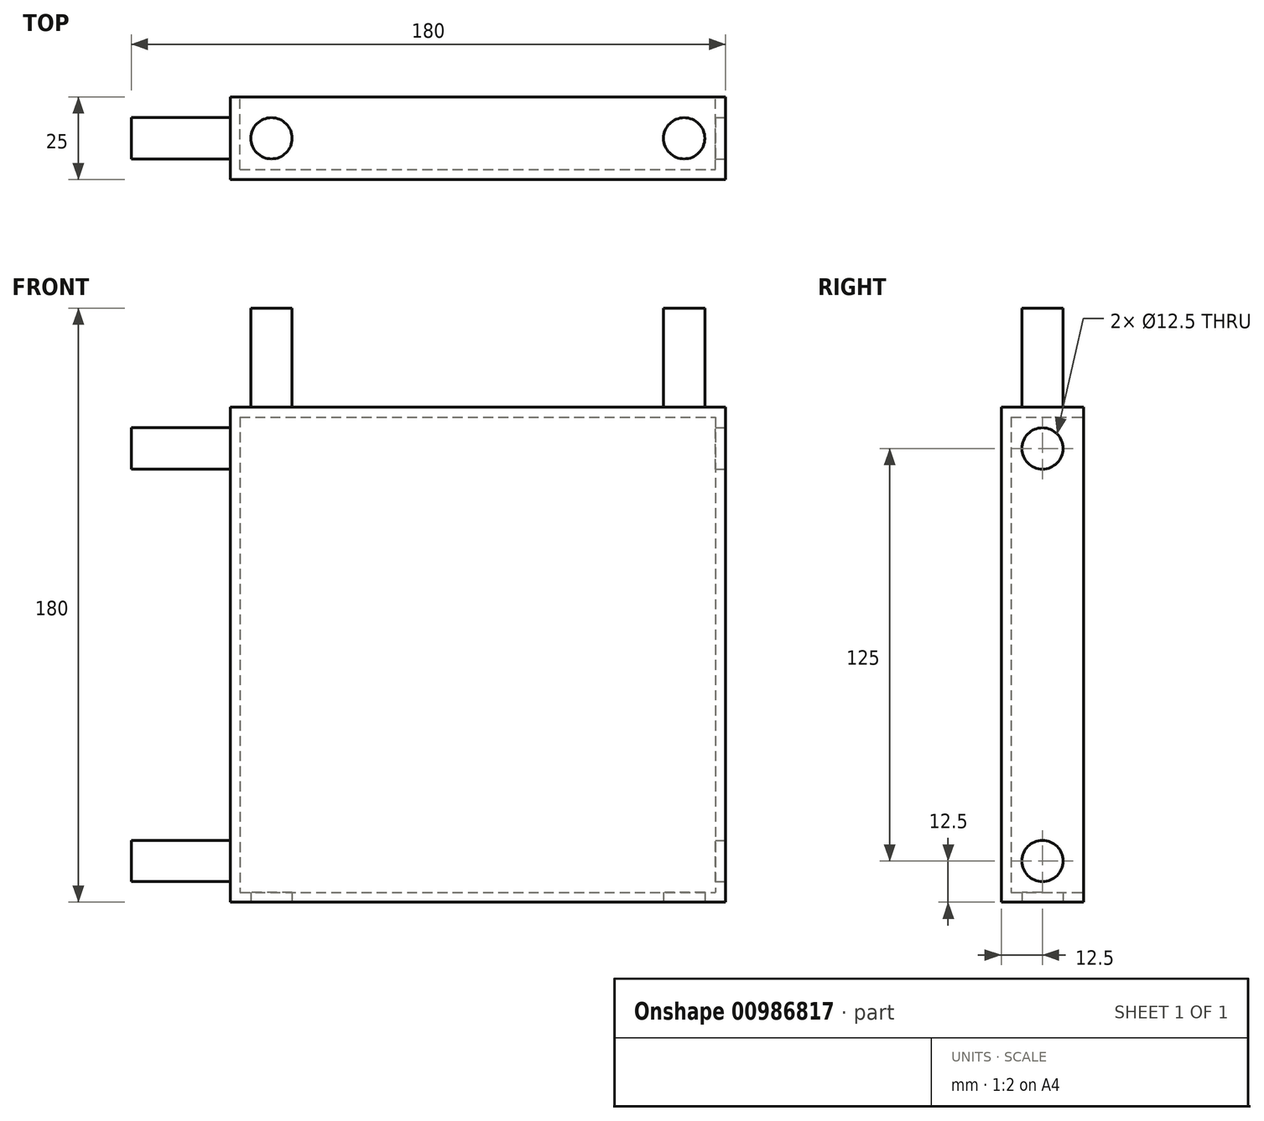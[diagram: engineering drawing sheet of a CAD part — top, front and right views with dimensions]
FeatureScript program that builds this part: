
annotation { "Feature Type Name" : "Feature", "Feature Type Description" : "" }
export const myFeature = defineFeature(function(context is Context, id is Id, definition is map)
    precondition{}
    {
        {
            var Q0;
            Q0=qCreatedBy(makeId("Front.planeOp"),FACE);
            var sketch = newSketch(context, id + "F0", { "sketchPlane" : qUnion([Q0])});
            skLineSegment(sketch, "E0.bottom", {"start": v(-87.46, 78.58) * mm, "end": v(62.54, 78.58) * mm});
            skLineSegment(sketch, "E0.top", {"start": v(-87.46, -71.42) * mm, "end": v(62.54, -71.42) * mm});
            skLineSegment(sketch, "E0.left", {"start": v(-87.46, 78.58) * mm, "end": v(-87.46, -71.42) * mm});
            skLineSegment(sketch, "E0.right", {"start": v(62.54, 78.58) * mm, "end": v(62.54, -71.42) * mm});
            skSolve(sketch);
        }
        {
            var Q0;
            Q0=makeQuery(id+"F0.imprint","IMPRINT",FACE,{"disambiguationData":[TD([[makeQuery(id+"F0.imprint","IMPRINT",EDGE,{"derivedFrom":sQuery(id+"F0.wireOp",EDGE,"E0.bottom")}),-1.0]])]});
            extrude(context, id + "F1", {"entities" : qUnion([Q0]), "depth" : 25 * mm, "offsetDistance" : 25 * mm});
        }
        {
            var Q0;
            Q0=makeQuery(id+"F1.opExtrude","CAP_FACE",FACE,{"disambiguationData":[OSD([sQuery(id+"F0.wireOp",EDGE,"E0.bottom"),sQuery(id+"F0.wireOp",EDGE,"E0.top"),sQuery(id+"F0.wireOp",EDGE,"E0.left"),sQuery(id+"F0.wireOp",EDGE,"E0.right")])],"isStart":true});
            shell(context, id + "F2", {"entities" : qUnion([Q0]), "thickness" : 3 * mm});
        }
        {
            var Q0;
            Q0=makeQuery(id+"F1.opExtrude","SWEPT_FACE",FACE,{"disambiguationData":[OSD([sQuery(id+"F0.wireOp",EDGE,"E0.bottom")])]});
            var sketch = newSketch(context, id + "F3", { "sketchPlane" : qUnion([Q0])});
            skCircle(sketch, "E1", {"center": v(-74.96, -12.5) * mm, "radius": 6.25 * mm});
            skCircle(sketch, "E2", {"center": v(50.04, -12.5) * mm, "radius": 6.25 * mm});
            skSolve(sketch);
        }
        {
            var Q0;
            Q0 = qSketchRegion(id + "F3", true);
            extrude(context, id + "F4", {"entities" : qUnion([Q0]), "operationType" : NewBodyOperationType.ADD, "depth" : 30 * mm, "offsetDistance" : 25 * mm});
        }
        {
            var Q0;
            Q0=makeQuery(id+"F1.opExtrude","SWEPT_FACE",FACE,{"disambiguationData":[OSD([sQuery(id+"F0.wireOp",EDGE,"E0.top")])]});
            var sketch = newSketch(context, id + "F5", { "sketchPlane" : qUnion([Q0])});
            skCircle(sketch, "E3", {"center": v(-74.96, 12.5) * mm, "radius": 6.25 * mm});
            skCircle(sketch, "E4", {"center": v(50.04, 12.5) * mm, "radius": 6.25 * mm});
            skSolve(sketch);
        }
        {
            var Q0;
            Q0 = qSketchRegion(id + "F5", true);
            extrude(context, id + "F6", {"entities" : qUnion([Q0]), "operationType" : NewBodyOperationType.REMOVE, "oppositeDirection" : true, "depth" : 25 * mm, "offsetDistance" : 25 * mm});
        }
        {
            var Q0;
            Q0=makeQuery(id+"F1.opExtrude","SWEPT_FACE",FACE,{"disambiguationData":[OSD([sQuery(id+"F0.wireOp",EDGE,"E0.left")])]});
            var sketch = newSketch(context, id + "F7", { "sketchPlane" : qUnion([Q0])});
            skCircle(sketch, "E5", {"center": v(12.5, 66.08) * mm, "radius": 6.25 * mm});
            skCircle(sketch, "E6", {"center": v(12.5, -58.92) * mm, "radius": 6.25 * mm});
            skSolve(sketch);
        }
        {
            var Q0;
            Q0 = qSketchRegion(id + "F7", true);
            extrude(context, id + "F8", {"entities" : qUnion([Q0]), "operationType" : NewBodyOperationType.ADD, "depth" : 30 * mm, "offsetDistance" : 25 * mm});
        }
        {
            var Q0;
            Q0=makeQuery(id+"F1.opExtrude","SWEPT_FACE",FACE,{"disambiguationData":[OSD([sQuery(id+"F0.wireOp",EDGE,"E0.right")])]});
            var sketch = newSketch(context, id + "F9", { "sketchPlane" : qUnion([Q0])});
            skCircle(sketch, "E7", {"center": v(-12.5, 66.08) * mm, "radius": 6.25 * mm});
            skCircle(sketch, "E8", {"center": v(-12.5, -58.92) * mm, "radius": 6.25 * mm});
            skSolve(sketch);
        }
        {
            var Q0;
            Q0 = qSketchRegion(id + "F9", true);
            extrude(context, id + "F10", {"entities" : qUnion([Q0]), "operationType" : NewBodyOperationType.REMOVE, "oppositeDirection" : true, "depth" : 30 * mm, "offsetDistance" : 25 * mm});
        }
    });
